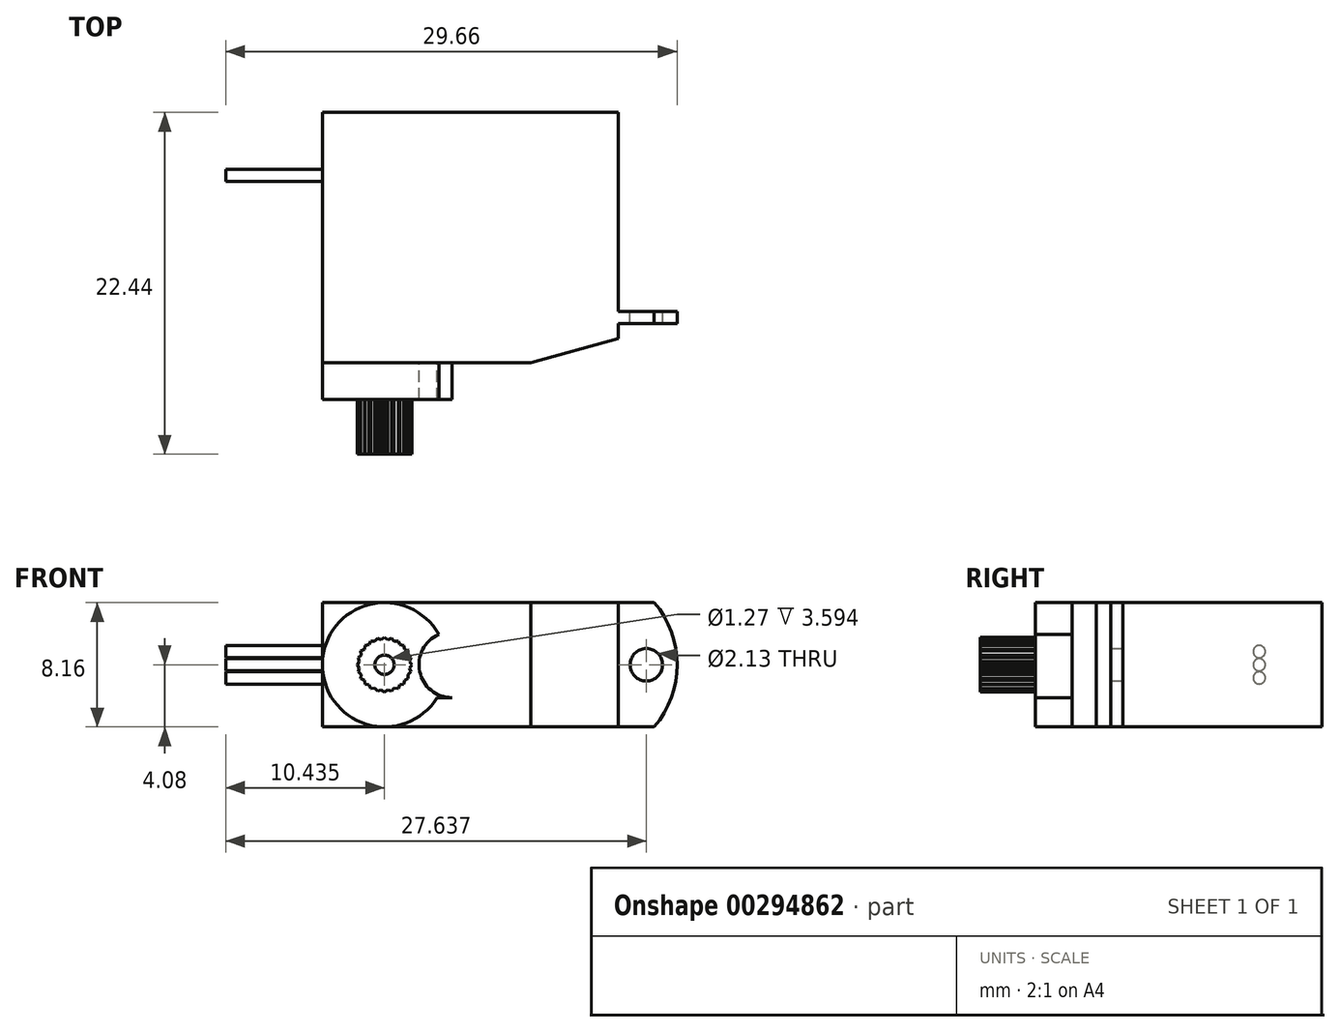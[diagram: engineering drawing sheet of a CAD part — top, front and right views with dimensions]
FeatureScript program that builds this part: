
annotation { "Feature Type Name" : "Feature", "Feature Type Description" : "" }
export const myFeature = defineFeature(function(context is Context, id is Id, definition is map)
    precondition{}
    {
        {
            var Q0;
            Q0=qCreatedBy(makeId("Front.planeOp"),FACE);
            var sketch = newSketch(context, id + "F0", { "sketchPlane" : qUnion([Q0])});
            skLineSegment(sketch, "E0.bottom", {"start": v(-9.73, 4.08) * mm, "end": v(9.73, 4.08) * mm});
            skLineSegment(sketch, "E0.top", {"start": v(-9.73, -4.08) * mm, "end": v(9.73, -4.08) * mm});
            skLineSegment(sketch, "E0.left", {"start": v(-9.73, 4.08) * mm, "end": v(-9.73, -4.08) * mm});
            skLineSegment(sketch, "E0.right", {"start": v(9.73, 4.08) * mm, "end": v(9.73, -4.08) * mm});
            skLineSegment(sketch, "E1", {"start": v(0, 4.08) * mm, "end": v(0, 0) * mm, "construction": true});
            skLineSegment(sketch, "E2", {"start": v(0, 0) * mm, "end": v(0, -4.08) * mm, "construction": true});
            skLineSegment(sketch, "E3", {"start": v(-9.73, 0) * mm, "end": v(0, 0) * mm, "construction": true});
            skLineSegment(sketch, "E4", {"start": v(0, 0) * mm, "end": v(9.73, 0) * mm, "construction": true});
            skSolve(sketch);
        }
        {
            var Q0;
            Q0=makeQuery(id+"F0.imprint","IMPRINT",FACE,{"disambiguationData":[TD([[makeQuery(id+"F0.imprint","IMPRINT",EDGE,{"derivedFrom":sQuery(id+"F0.wireOp",EDGE,"E0.bottom")}),-1.0]])]});
            extrude(context, id + "F1", {"entities" : qUnion([Q0]), "depth" : 16.43 * mm});
        }
        {
            var Q0;
            Q0=makeQuery(id+"F1.opExtrude","SWEPT_FACE",FACE,{"disambiguationData":[OSD([sQuery(id+"F0.wireOp",EDGE,"E0.top")])]});
            var sketch = newSketch(context, id + "F2", { "sketchPlane" : qUnion([Q0])});
            skLineSegment(sketch, "E5", {"start": v(9.73, 14.83) * mm, "end": v(3.98, 16.43) * mm});
            skLineSegment(sketch, "E6", {"start": v(3.98, 16.43) * mm, "end": v(9.73, 16.43) * mm});
            skLineSegment(sketch, "E7", {"start": v(9.73, 16.43) * mm, "end": v(9.73, 14.83) * mm});
            skSolve(sketch);
        }
        {
            var Q0;
            Q0=makeQuery(id+"F2.imprint","IMPRINT",FACE,{"disambiguationData":[TD([[makeQuery(id+"F2.imprint","IMPRINT",EDGE,{"derivedFrom":sQuery(id+"F2.wireOp",EDGE,"E5")}),-1.0]])]});
            var Q1;
            Q1=makeQuery(id+"F1.opExtrude","SWEPT_FACE",FACE,{"disambiguationData":[OSD([sQuery(id+"F0.wireOp",EDGE,"E0.bottom")])]});
            extrude(context, id + "F3", {"entities" : qUnion([Q0]), "operationType" : NewBodyOperationType.REMOVE, "endBound" : BoundingType.UP_TO_SURFACE, "oppositeDirection" : true, "endBoundEntityFace" : qUnion([Q1]), "depth" : 25.4 * mm});
        }
        {
            var Q0;
            Q0=makeQuery(id+"F1.opExtrude","CAP_FACE",FACE,{"disambiguationData":[OSD([sQuery(id+"F0.wireOp",EDGE,"E0.bottom"),sQuery(id+"F0.wireOp",EDGE,"E0.top"),sQuery(id+"F0.wireOp",EDGE,"E0.left"),sQuery(id+"F0.wireOp",EDGE,"E0.right")])],"isStart":false});
            var sketch = newSketch(context, id + "F4", { "sketchPlane" : qUnion([Q0])});
            skCircle(sketch, "E8", {"center": v(-5.65, 0) * mm, "radius": 4.08 * mm});
            skCircle(sketch, "E9", {"center": v(-1.22, 0) * mm, "radius": 2.16 * mm});
            skLineSegment(sketch, "E10", {"start": v(-1.22, 2.16) * mm, "end": v(-2.18, 2.16) * mm});
            skLineSegment(sketch, "E11", {"start": v(-1.22, -2.16) * mm, "end": v(-2.18, -2.16) * mm});
            skSolve(sketch);
        }
        {
            var Q0;
            {var subQ0=sQuery(id+"F4.wireOp",EDGE,"E8");var subQ4=makeQuery(id+"F4.imprint","INTERSECT",VERTEX,{"derivedFrom":[subQ0,sQuery(id+"F4.wireOp",EDGE,"E10")]});Q0=makeQuery(id+"F4.imprint","IMPRINT",FACE,{"disambiguationData":[TD([[makeQuery(id+"F4.imprint","IMPRINT",EDGE,{"disambiguationData":[TD([[subQ4,1.0]])],"derivedFrom":subQ0}),1.0]])]});}
            var Q1;
            {var subQ0=sQuery(id+"F4.wireOp",EDGE,"E9");var subQ1=sQuery(id+"F4.wireOp",EDGE,"E8");var subQ2=makeQuery(id+"F4.imprint","INTERSECT",VERTEX,{"disambiguationData":[OD(0.0)],"derivedFrom":[subQ1,subQ0]});Q1=makeQuery(id+"F4.imprint","IMPRINT",FACE,{"disambiguationData":[TD([[makeQuery(id+"F4.imprint","IMPRINT",EDGE,{"disambiguationData":[TD([[subQ2,1.0]])],"derivedFrom":subQ1}),1.0]])]});}
            var Q2;
            {var subQ0=sQuery(id+"F4.wireOp",EDGE,"E9");var subQ1=sQuery(id+"F4.wireOp",EDGE,"E8");var subQ2=makeQuery(id+"F4.imprint","INTERSECT",VERTEX,{"disambiguationData":[OD(0.0)],"derivedFrom":[subQ1,subQ0]});Q2=makeQuery(id+"F4.imprint","IMPRINT",FACE,{"disambiguationData":[TD([[makeQuery(id+"F4.imprint","IMPRINT",EDGE,{"disambiguationData":[TD([[subQ2,1.0]])],"derivedFrom":subQ1}),-1.0]])]});}
            extrude(context, id + "F5", {"entities" : qUnion([Q0, Q1, Q2]), "operationType" : NewBodyOperationType.ADD, "depth" : 2.41 * mm});
        }
        {
            var Q0;
            Q0=makeQuery(id+"F5.opExtrude","CAP_FACE",FACE,{"disambiguationData":[OSD([sQuery(id+"F4.wireOp",EDGE,"E8"),sQuery(id+"F4.wireOp",EDGE,"E9")])],"isStart":false});
            var sketch = newSketch(context, id + "F6", { "sketchPlane" : qUnion([Q0])});
            skCircle(sketch, "E12", {"center": v(-5.65, 0) * mm, "radius": 1.8 * mm, "construction": true});
            skCircle(sketch, "E13", {"center": v(-5.65, 0) * mm, "radius": 1.67 * mm, "construction": true});
            skLineSegment(sketch, "E14", {"start": v(-5.65, 0) * mm, "end": v(-5.65, 1.8) * mm, "construction": true});
            skLineSegment(sketch, "E15", {"start": v(-5.65, 1.8) * mm, "end": v(-5.86, 1.66) * mm});
            skLineSegment(sketch, "E16", {"start": v(-5.65, 1.8) * mm, "end": v(-5.43, 1.66) * mm});
            skLineSegment(sketch, "E17", {"start": v(-5.86, 1.66) * mm, "end": v(-5.65, 0) * mm, "construction": true});
            skLineSegment(sketch, "E18", {"start": v(-5.65, 0) * mm, "end": v(-5.43, 1.66) * mm, "construction": true});
            skLineSegment(sketch, "E19.1.0", {"start": v(-6.11, 1.74) * mm, "end": v(-5.86, 1.66) * mm});
            skLineSegment(sketch, "E19.1.1", {"start": v(-6.11, 1.74) * mm, "end": v(-6.28, 1.54) * mm});
            skLineSegment(sketch, "E19.2.0", {"start": v(-6.54, 1.56) * mm, "end": v(-6.28, 1.54) * mm});
            skLineSegment(sketch, "E19.2.1", {"start": v(-6.54, 1.56) * mm, "end": v(-6.66, 1.32) * mm});
            skLineSegment(sketch, "E19.3.0", {"start": v(-6.92, 1.27) * mm, "end": v(-6.66, 1.32) * mm});
            skLineSegment(sketch, "E19.3.1", {"start": v(-6.92, 1.27) * mm, "end": v(-6.97, 1.02) * mm});
            skLineSegment(sketch, "E19.4.0", {"start": v(-7.2, 0.9) * mm, "end": v(-6.97, 1.02) * mm});
            skLineSegment(sketch, "E19.4.1", {"start": v(-7.2, 0.9) * mm, "end": v(-7.19, 0.64) * mm});
            skLineSegment(sketch, "E19.5.0", {"start": v(-7.38, 0.47) * mm, "end": v(-7.19, 0.64) * mm});
            skLineSegment(sketch, "E19.5.1", {"start": v(-7.38, 0.47) * mm, "end": v(-7.3, 0.22) * mm});
            skLineSegment(sketch, "E19.6.0", {"start": v(-7.44, 0) * mm, "end": v(-7.3, 0.22) * mm});
            skLineSegment(sketch, "E19.6.1", {"start": v(-7.44, 0) * mm, "end": v(-7.3, -0.22) * mm});
            skLineSegment(sketch, "E19.7.0", {"start": v(-7.38, -0.47) * mm, "end": v(-7.3, -0.22) * mm});
            skLineSegment(sketch, "E19.7.1", {"start": v(-7.38, -0.47) * mm, "end": v(-7.19, -0.64) * mm});
            skLineSegment(sketch, "E19.8.0", {"start": v(-7.2, -0.9) * mm, "end": v(-7.19, -0.64) * mm});
            skLineSegment(sketch, "E19.8.1", {"start": v(-7.2, -0.9) * mm, "end": v(-6.97, -1.02) * mm});
            skLineSegment(sketch, "E19.9.0", {"start": v(-6.92, -1.27) * mm, "end": v(-6.97, -1.02) * mm});
            skLineSegment(sketch, "E19.9.1", {"start": v(-6.92, -1.27) * mm, "end": v(-6.66, -1.32) * mm});
            skLineSegment(sketch, "E19.10.0", {"start": v(-6.54, -1.56) * mm, "end": v(-6.66, -1.32) * mm});
            skLineSegment(sketch, "E19.10.1", {"start": v(-6.54, -1.56) * mm, "end": v(-6.28, -1.54) * mm});
            skLineSegment(sketch, "E19.11.0", {"start": v(-6.11, -1.74) * mm, "end": v(-6.28, -1.54) * mm});
            skLineSegment(sketch, "E19.11.1", {"start": v(-6.11, -1.74) * mm, "end": v(-5.86, -1.66) * mm});
            skLineSegment(sketch, "E19.12.0", {"start": v(-5.65, -1.8) * mm, "end": v(-5.86, -1.66) * mm});
            skLineSegment(sketch, "E19.12.1", {"start": v(-5.65, -1.8) * mm, "end": v(-5.43, -1.66) * mm});
            skLineSegment(sketch, "E19.13.0", {"start": v(-5.18, -1.74) * mm, "end": v(-5.43, -1.66) * mm});
            skLineSegment(sketch, "E19.13.1", {"start": v(-5.18, -1.74) * mm, "end": v(-5, -1.54) * mm});
            skLineSegment(sketch, "E19.14.0", {"start": v(-4.75, -1.56) * mm, "end": v(-5, -1.54) * mm});
            skLineSegment(sketch, "E19.14.1", {"start": v(-4.75, -1.56) * mm, "end": v(-4.63, -1.32) * mm});
            skLineSegment(sketch, "E19.15.0", {"start": v(-4.37, -1.27) * mm, "end": v(-4.63, -1.32) * mm});
            skLineSegment(sketch, "E19.15.1", {"start": v(-4.37, -1.27) * mm, "end": v(-4.32, -1.02) * mm});
            skLineSegment(sketch, "E19.16.0", {"start": v(-4.09, -0.9) * mm, "end": v(-4.32, -1.02) * mm});
            skLineSegment(sketch, "E19.16.1", {"start": v(-4.09, -0.9) * mm, "end": v(-4.1, -0.64) * mm});
            skLineSegment(sketch, "E19.17.0", {"start": v(-3.9, -0.47) * mm, "end": v(-4.1, -0.64) * mm});
            skLineSegment(sketch, "E19.17.1", {"start": v(-3.9, -0.47) * mm, "end": v(-3.99, -0.22) * mm});
            skLineSegment(sketch, "E19.18.0", {"start": v(-3.85, 0) * mm, "end": v(-3.99, -0.22) * mm});
            skLineSegment(sketch, "E19.18.1", {"start": v(-3.85, 0) * mm, "end": v(-3.99, 0.22) * mm});
            skLineSegment(sketch, "E19.19.0", {"start": v(-3.9, 0.47) * mm, "end": v(-3.99, 0.22) * mm});
            skLineSegment(sketch, "E19.19.1", {"start": v(-3.9, 0.47) * mm, "end": v(-4.1, 0.64) * mm});
            skLineSegment(sketch, "E19.20.0", {"start": v(-4.09, 0.9) * mm, "end": v(-4.1, 0.64) * mm});
            skLineSegment(sketch, "E19.20.1", {"start": v(-4.09, 0.9) * mm, "end": v(-4.32, 1.02) * mm});
            skLineSegment(sketch, "E19.21.0", {"start": v(-4.37, 1.27) * mm, "end": v(-4.32, 1.02) * mm});
            skLineSegment(sketch, "E19.21.1", {"start": v(-4.37, 1.27) * mm, "end": v(-4.63, 1.32) * mm});
            skLineSegment(sketch, "E19.22.0", {"start": v(-4.75, 1.56) * mm, "end": v(-4.63, 1.32) * mm});
            skLineSegment(sketch, "E19.22.1", {"start": v(-4.75, 1.56) * mm, "end": v(-5, 1.54) * mm});
            skLineSegment(sketch, "E19.23.0", {"start": v(-5.18, 1.74) * mm, "end": v(-5, 1.54) * mm});
            skLineSegment(sketch, "E19.23.1", {"start": v(-5.18, 1.74) * mm, "end": v(-5.43, 1.66) * mm});
            skCircle(sketch, "E20", {"center": v(-5.65, 0) * mm, "radius": 0.64 * mm});
            skSolve(sketch);
        }
        {
            var Q0;
            Q0=makeQuery(id+"F6.imprint","IMPRINT",FACE,{"disambiguationData":[TD([[makeQuery(id+"F6.imprint","IMPRINT",EDGE,{"derivedFrom":sQuery(id+"F6.wireOp",EDGE,"E15")}),1.0]])]});
            extrude(context, id + "F7", {"entities" : qUnion([Q0]), "operationType" : NewBodyOperationType.ADD, "depth" : 3.6 * mm});
        }
        {
            var Q0;
            {var subQ0=sQuery(id+"F0.wireOp",EDGE,"E0.top");var subQ1=sQuery(id+"F0.wireOp",EDGE,"E0.bottom");var subQ2=makeQuery(id+"F1.opExtrude","CAP_FACE",FACE,{"disambiguationData":[OSD([subQ1,subQ0,sQuery(id+"F0.wireOp",EDGE,"E0.left"),sQuery(id+"F0.wireOp",EDGE,"E0.right")])],"isStart":false});Q0=makeQuery(id+"F5.boolean.opBoolean","SPLIT",FACE,{"disambiguationData":[TD([makeQuery(id+"F1.opExtrude","SWEPT_FACE",FACE,{"disambiguationData":[OSD([subQ1])]}),subQ2,makeQuery(id+"F1.opExtrude","SWEPT_FACE",FACE,{"disambiguationData":[OSD([subQ0])]}),makeQuery(id+"F3.boolean.opBoolean","COPY",FACE,{"derivedFrom":makeQuery(id+"F3.opExtrude","SWEPT_FACE",FACE,{"disambiguationData":[OSD([sQuery(id+"F2.wireOp",EDGE,"E5")])]})}),makeQuery(id+"F5.opExtrude","SWEPT_FACE",FACE,{"disambiguationData":[OSD([sQuery(id+"F4.wireOp",EDGE,"E8")])]}),makeQuery(id+"F5.opExtrude","SWEPT_FACE",FACE,{"disambiguationData":[OSD([sQuery(id+"F4.wireOp",EDGE,"E9")])]})])],"derivedFrom":subQ2});}
            cPlane(context, id + "F8", {"entities" : qUnion([Q0]), "cplaneType" : CPlaneType.OFFSET, "offset" : 3.35 * mm, "oppositeDirection" : true, "width" : 152.4 * mm, "height" : 152.4 * mm});
        }
        {
            var Q0;
            Q0=qCreatedBy(id+"F8.planeOp",FACE);
            var sketch = newSketch(context, id + "F9", { "sketchPlane" : qUnion([Q0])});
            skLineSegment(sketch, "E21.bottom", {"start": v(9.73, 4.08) * mm, "end": v(12.08, 4.08) * mm});
            skLineSegment(sketch, "E21.top", {"start": v(9.73, -4.08) * mm, "end": v(12.08, -4.08) * mm});
            skLineSegment(sketch, "E21.left", {"start": v(9.73, 4.08) * mm, "end": v(9.73, -4.08) * mm});
            skLineSegment(sketch, "E21.right", {"start": v(12.08, 4.08) * mm, "end": v(12.08, -4.08) * mm, "construction": true});
            skArc(sketch, "E22", {"start": v(12.08, -4.08) * mm, "mid": v(13.58, 0) * mm, "end": v(12.08, 4.08) * mm});
            skCircle(sketch, "E23", {"center": v(11.56, 0) * mm, "radius": 1.07 * mm});
            skPoint(sketch, "E23.centerSnap0", {"position": v(12.08, 0) * mm});
            skSolve(sketch);
        }
        {
            var Q0;
            Q0=makeQuery(id+"F9.imprint","IMPRINT",FACE,{"disambiguationData":[TD([[makeQuery(id+"F9.imprint","IMPRINT",EDGE,{"derivedFrom":sQuery(id+"F9.wireOp",EDGE,"E21.bottom")}),-1.0]])]});
            extrude(context, id + "F10", {"entities" : qUnion([Q0]), "operationType" : NewBodyOperationType.ADD, "depth" : 0.79 * mm});
        }
        {
            var Q0;
            {var subQ2=sQuery(id+"F0.wireOp",EDGE,"E0.top");var subQ3=sQuery(id+"F0.wireOp",EDGE,"E0.left");var subQ4=sQuery(id+"F0.wireOp",EDGE,"E0.bottom");Q0=makeQuery(id+"FjOupoCfuzc5YXj_1.1.F10.boolean.opBoolean","SPLIT",FACE,{"disambiguationData":[TD([makeQuery(id+"F1.opExtrude","CAP_FACE",FACE,{"disambiguationData":[OSD([subQ4,subQ2,subQ3,sQuery(id+"F0.wireOp",EDGE,"E0.right")])],"isStart":true})])],"derivedFrom":makeQuery(id+"F1.opExtrude","SWEPT_FACE",FACE,{"disambiguationData":[OSD([subQ3])]})});}
            var sketch = newSketch(context, id + "F11", { "sketchPlane" : qUnion([Q0])});
            skCircle(sketch, "E24", {"center": v(4.13, 0.86) * mm, "radius": 0.4 * mm});
            skCircle(sketch, "E25", {"center": v(4.13, 0) * mm, "radius": 0.4 * mm});
            skCircle(sketch, "E26", {"center": v(4.13, -0.86) * mm, "radius": 0.4 * mm});
            skLineSegment(sketch, "E27", {"start": v(4.13, -0.86) * mm, "end": v(4.13, 0) * mm, "construction": true});
            skLineSegment(sketch, "E28", {"start": v(4.13, 0.86) * mm, "end": v(4.13, 0) * mm, "construction": true});
            skSolve(sketch);
        }
        {
            var Q0;
            Q0=makeQuery(id+"F11.imprint","IMPRINT",FACE,{"disambiguationData":[TD([[makeQuery(id+"F11.imprint","IMPRINT",EDGE,{"derivedFrom":sQuery(id+"F11.wireOp",EDGE,"E24")}),1.0]])]});
            var Q1;
            Q1=makeQuery(id+"F11.imprint","IMPRINT",FACE,{"disambiguationData":[TD([[makeQuery(id+"F11.imprint","IMPRINT",EDGE,{"derivedFrom":sQuery(id+"F11.wireOp",EDGE,"E25")}),1.0]])]});
            var Q2;
            Q2=makeQuery(id+"F11.imprint","IMPRINT",FACE,{"disambiguationData":[TD([[makeQuery(id+"F11.imprint","IMPRINT",EDGE,{"derivedFrom":sQuery(id+"F11.wireOp",EDGE,"E26")}),1.0]])]});
            extrude(context, id + "F12", {"entities" : qUnion([Q0, Q1, Q2]), "operationType" : NewBodyOperationType.ADD, "depth" : 6.35 * mm});
        }
    });
